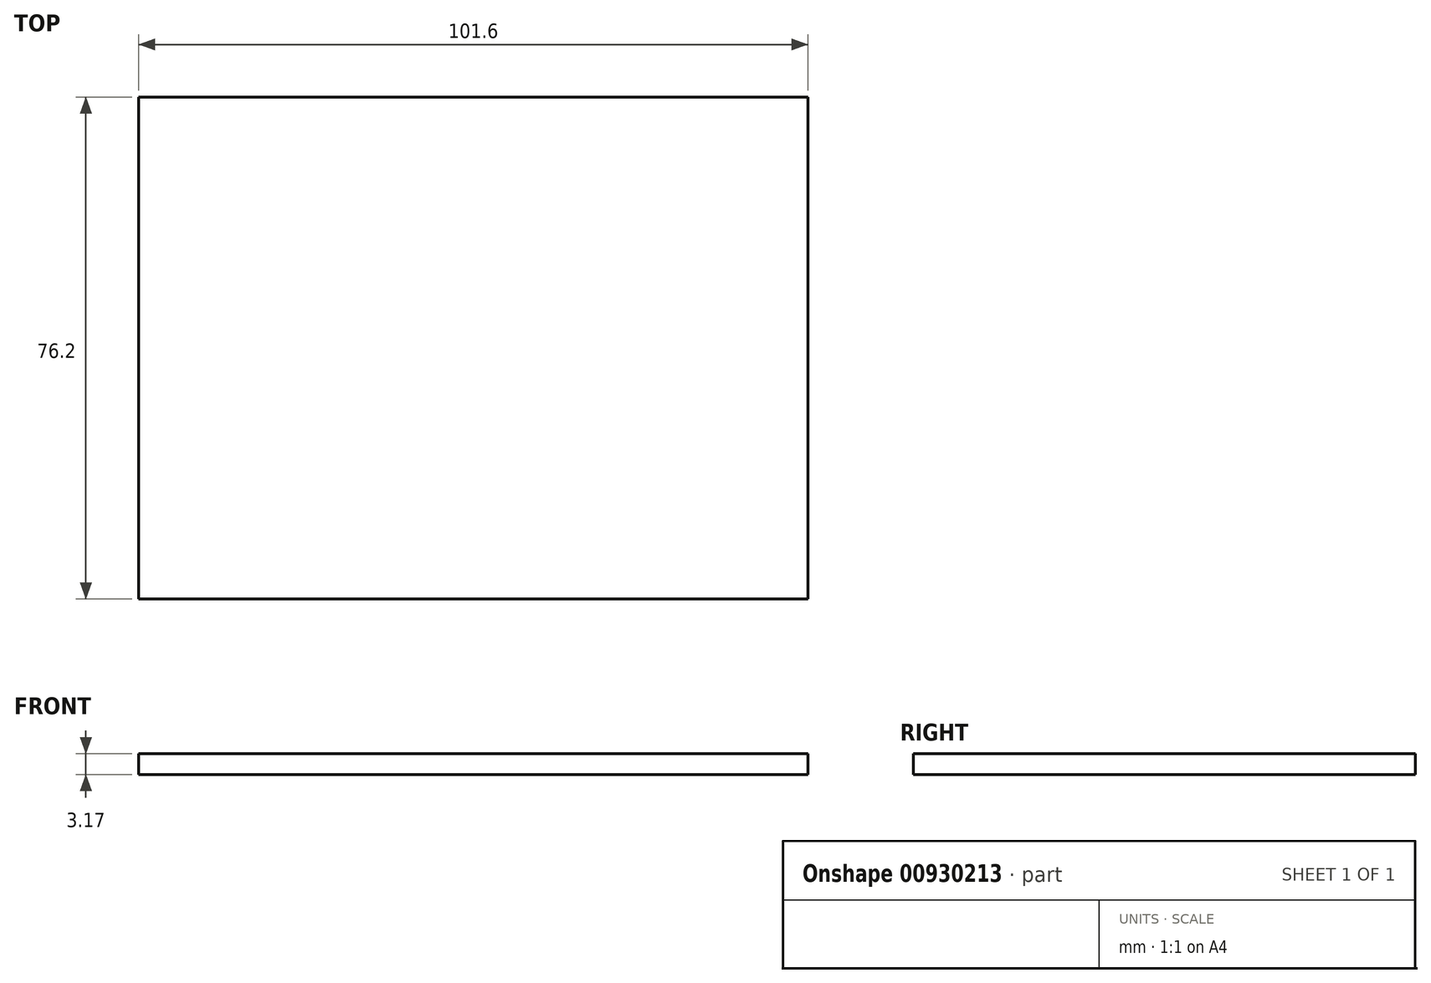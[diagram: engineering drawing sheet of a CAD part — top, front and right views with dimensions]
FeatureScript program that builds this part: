
annotation { "Feature Type Name" : "Feature", "Feature Type Description" : "" }
export const myFeature = defineFeature(function(context is Context, id is Id, definition is map)
    precondition{}
    {
        {
            var Q0;
            Q0=qCreatedBy(makeId("Top.planeOp"),FACE);
            var sketch = newSketch(context, id + "F0", { "sketchPlane" : qUnion([Q0])});
            skLineSegment(sketch, "E0.bottom", {"start": v(19.86, -12.46) * mm, "end": v(-81.74, -12.46) * mm});
            skLineSegment(sketch, "E0.top", {"start": v(19.86, 63.74) * mm, "end": v(-81.74, 63.74) * mm});
            skLineSegment(sketch, "E0.left", {"start": v(19.86, -12.46) * mm, "end": v(19.86, 63.74) * mm});
            skLineSegment(sketch, "E0.right", {"start": v(-81.74, -12.46) * mm, "end": v(-81.74, 63.74) * mm});
            skPoint(sketch, "E0.middle", {"position": v(-30.94, 25.64) * mm});
            skSolve(sketch);
        }
        {
            var Q0;
            Q0=makeQuery(id+"F0.imprint","IMPRINT",FACE,{"disambiguationData":[TD([[makeQuery(id+"F0.imprint","IMPRINT",EDGE,{"derivedFrom":sQuery(id+"F0.wireOp",EDGE,"E0.bottom")}),-1.0]])]});
            extrude(context, id + "F1", {"entities" : qUnion([Q0]), "depth" : 3.17 * mm, "offsetDistance" : 25.4 * mm});
        }
    });
